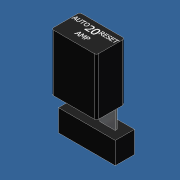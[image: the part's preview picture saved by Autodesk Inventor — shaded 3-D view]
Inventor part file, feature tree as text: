
AUTODESK INVENTOR PART (.ipt)
format: ipt  version: 2012 (Build 160160000, 160)  size: 334,336 bytes
history: native  units: mm (DEFAULTED — no unit token found)
features: extrude x4, sketch x4, plane x3
ambient origin geometry x5: Origin, X Axis, Y Axis, Z Axis, Center Point
bodies: Solid1 (feature_tree)
feature tree (11):
  extrude  "Extrusion1"  Depth=9.906mm
  extrude  "Extrusion2"  Depth=19.812mm TaperAngle=0.0deg
  extrude  "Extrusion3"  Depth=5.3848mm
  extrude  "Extrusion4"  Depth=2.9718mm
  plane  "YZ Plane (RIGHT)"
  plane  "XZ Plane (TOP)"
  plane  "XY Plane (FRONT)"
  sketch  "Sketch2"  dims[d0=15.748mm d1=9.906mm]
  sketch  "Sketch3"  dims[d2=0.762mm d3=19.812mm d4=0.0mm]
  sketch  "Sketch4"  dims[d5=0.7112mm d6=5.3848mm]
  sketch  "Sketch5"  dims[d7=7.874mm d8=2.9718mm d9=14.478mm d10=0.0mm d11=34.6964mm d12=6.7056mm d13=7.62mm d14=19.812mm d15=0.0mm d16=0.00254mm d17=0.0mm]
